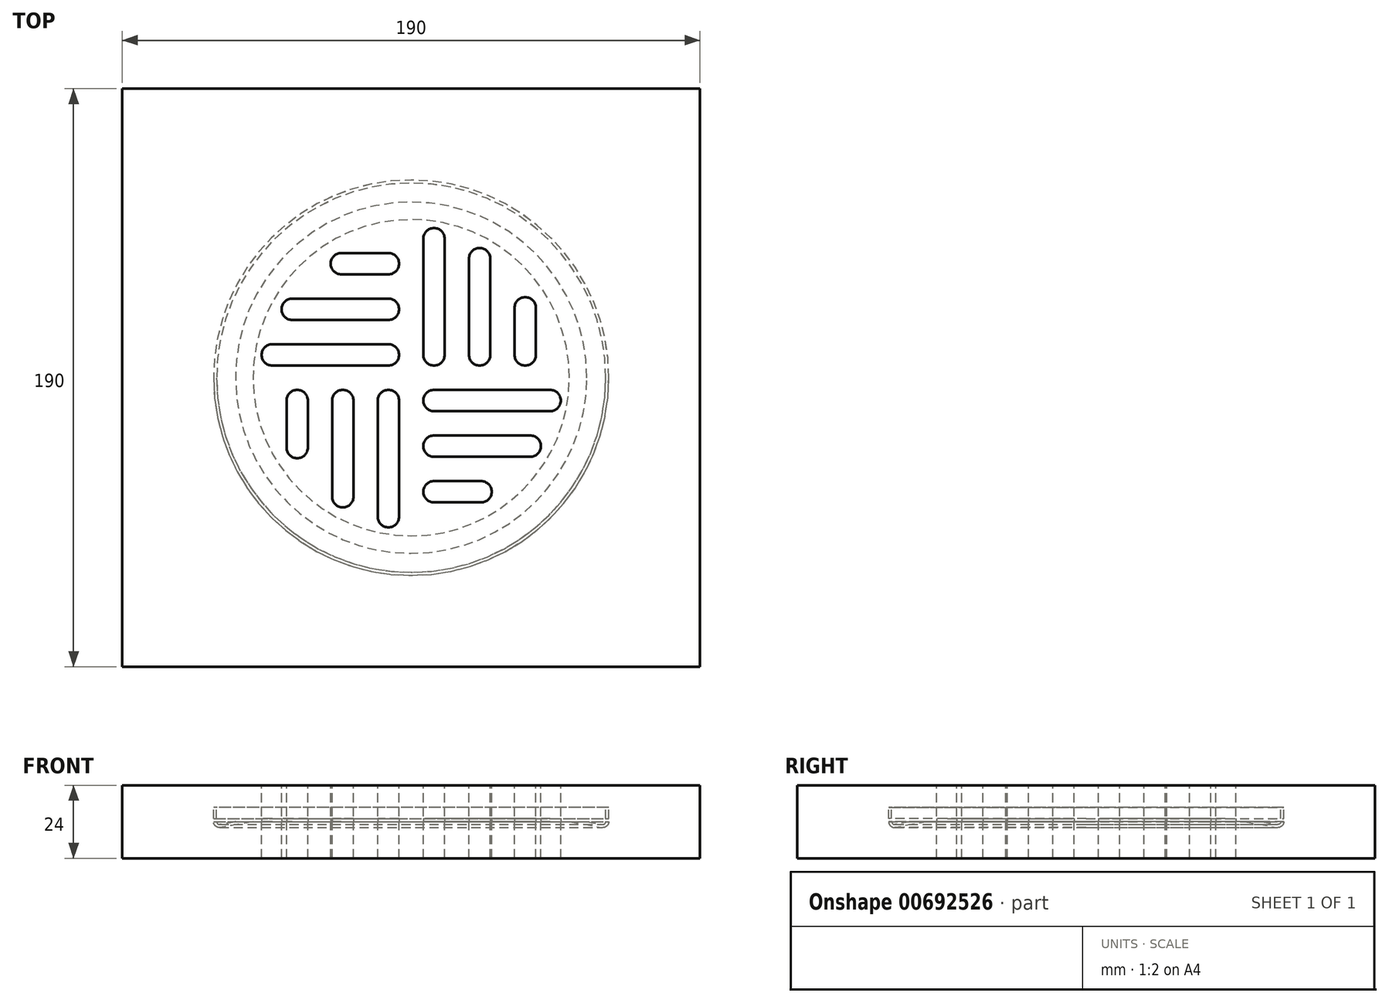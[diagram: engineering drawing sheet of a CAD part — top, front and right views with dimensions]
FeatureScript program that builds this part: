
annotation { "Feature Type Name" : "Feature", "Feature Type Description" : "" }
export const myFeature = defineFeature(function(context is Context, id is Id, definition is map)
    precondition{}
    {
        {
            var Q0;
            Q0=qCreatedBy(makeId("Top.planeOp"),FACE);
            var sketch = newSketch(context, id + "F0", { "sketchPlane" : qUnion([Q0])});
            skLineSegment(sketch, "E0", {"start": v(20.45, 0) * mm, "end": v(50.59, 0) * mm});
            skLineSegment(sketch, "E1", {"start": v(50.59, 0) * mm, "end": v(50.59, 2.78) * mm});
            skLineSegment(sketch, "E2", {"start": v(20.45, 0) * mm, "end": v(20.45, 3.6) * mm});
            skLineSegment(sketch, "E3", {"start": v(20.45, 3.6) * mm, "end": v(16.3, 3.6) * mm});
            skLineSegment(sketch, "E4", {"start": v(16.3, 3.6) * mm, "end": v(16.3, 7.46) * mm});
            skLineSegment(sketch, "E5", {"start": v(16.3, 7.46) * mm, "end": v(12.16, 7.46) * mm});
            skLineSegment(sketch, "E6.0", {"start": v(16.9, 8.06) * mm, "end": v(12.16, 8.06) * mm});
            skLineSegment(sketch, "E6.1", {"start": v(16.9, 4.2) * mm, "end": v(16.9, 8.06) * mm});
            skLineSegment(sketch, "E6.2", {"start": v(49.99, 0.6) * mm, "end": v(49.99, 2.78) * mm});
            skLineSegment(sketch, "E6.3", {"start": v(21.05, 0.6) * mm, "end": v(49.99, 0.6) * mm});
            skLineSegment(sketch, "E6.4", {"start": v(21.05, 0.6) * mm, "end": v(21.05, 4.2) * mm});
            skLineSegment(sketch, "E6.5", {"start": v(21.05, 4.2) * mm, "end": v(16.9, 4.2) * mm});
            skLineSegment(sketch, "E7", {"start": v(12.16, 8.06) * mm, "end": v(12.16, 7.46) * mm});
            skLineSegment(sketch, "E8", {"start": v(49.99, 2.78) * mm, "end": v(50.59, 2.78) * mm});
            skSolve(sketch);
        }
        {
            var Q0;
            Q0=qCreatedBy(makeId("Top.planeOp"),FACE);
            var sketch = newSketch(context, id + "F1", { "sketchPlane" : qUnion([Q0])});
            skLineSegment(sketch, "E9", {"start": v(0, 12.91) * mm, "end": v(0, -2.1) * mm, "construction": true});
            skSolve(sketch);
        }
        {
            var Q0;
            Q0=makeQuery(id+"F0.imprint","IMPRINT",FACE,{"disambiguationData":[TD([[makeQuery(id+"F0.imprint","IMPRINT",EDGE,{"derivedFrom":sQuery(id+"F0.wireOp",EDGE,"E0")}),1.0]])]});
            var Q1;
            Q1=sQuery(id+"F1.wireOp",EDGE,"E9");
            revolve(context, id + "F2", {"entities" : qUnion([Q0]), "axis" : qUnion([Q1]), "revolveType" : RevolveType.FULL});
        }
        {
            var Q0;
            Q0=makeQuery(id+"F2.opRevolve","SWEPT_BODY",BODY,{"disambiguationData":[OSD([sQuery(id+"F0.wireOp",EDGE,"E0"),sQuery(id+"F0.wireOp",EDGE,"E1"),sQuery(id+"F0.wireOp",EDGE,"E2"),sQuery(id+"F0.wireOp",EDGE,"E3"),sQuery(id+"F0.wireOp",EDGE,"E4"),sQuery(id+"F0.wireOp",EDGE,"E5"),sQuery(id+"F0.wireOp",EDGE,"E6.0"),sQuery(id+"F0.wireOp",EDGE,"E6.1"),sQuery(id+"F0.wireOp",EDGE,"E6.2"),sQuery(id+"F0.wireOp",EDGE,"E6.3"),sQuery(id+"F0.wireOp",EDGE,"E6.4"),sQuery(id+"F0.wireOp",EDGE,"E6.5"),sQuery(id+"F0.wireOp",EDGE,"E7"),sQuery(id+"F0.wireOp",EDGE,"E8")])]});
            deleteBodies(context, id + "F3", {"entities" : qUnion([Q0])});
        }
        {
            var Q0;
            Q0=qCreatedBy(makeId("Front.planeOp"),FACE);
            var sketch = newSketch(context, id + "F4", { "sketchPlane" : qUnion([Q0])});
            skLineSegment(sketch, "E10", {"start": v(0, 57.85) * mm, "end": v(0, -62.15) * mm, "construction": true});
            skLineSegment(sketch, "E11", {"start": v(-52, 0) * mm, "end": v(0, 0) * mm});
            skLineSegment(sketch, "E12", {"start": v(-52, 0) * mm, "end": v(-62.65, -1.88) * mm});
            skLineSegment(sketch, "E13", {"start": v(-65, 4.7) * mm, "end": v(-65, 0.1) * mm});
            skPoint(sketch, "E14.visualSharp", {"position": v(-65, -2.3) * mm});
            skArc(sketch, "E14.filletArc", {"start": v(-65, 0.1) * mm, "mid": v(-64.29, -1.44) * mm, "end": v(-62.65, -1.88) * mm});
            skLineSegment(sketch, "E15.0", {"start": v(-52.09, 1) * mm, "end": v(0, 1) * mm});
            skLineSegment(sketch, "E15.1", {"start": v(-52.09, 1) * mm, "end": v(-62.83, -0.9) * mm});
            skLineSegment(sketch, "E15.2", {"start": v(-64, 4.7) * mm, "end": v(-64, 0.1) * mm});
            skPoint(sketch, "E16.visualSharp", {"position": v(-64, -1.1) * mm});
            skArc(sketch, "E16.filletArc", {"start": v(-64, 0.1) * mm, "mid": v(-63.64, -0.67) * mm, "end": v(-62.83, -0.9) * mm});
            skLineSegment(sketch, "E17", {"start": v(-65, 4.7) * mm, "end": v(-64, 4.7) * mm});
            skLineSegment(sketch, "E18", {"start": v(0, 1) * mm, "end": v(0, 0) * mm});
            skSolve(sketch);
        }
        {
            var Q0;
            Q0=qSketchRegion(id+"F4",true);
            var Q1;
            Q1=sQuery(id+"F4.wireOp",EDGE,"E10");
            revolve(context, id + "F5", {"entities" : qUnion([Q0]), "axis" : qUnion([Q1]), "revolveType" : RevolveType.FULL});
        }
        {
            var Q0;
            Q0=makeQuery(id+"F5.opRevolve","SWEPT_FACE",FACE,{"disambiguationData":[OSD([sQuery(id+"F4.wireOp",EDGE,"E11")])]});
            var sketch = newSketch(context, id + "F6", { "sketchPlane" : qUnion([Q0])});
            skLineSegment(sketch, "E19.left", {"start": v(-11, 45.7) * mm, "end": v(-11, 7.5) * mm});
            skLineSegment(sketch, "E19.right", {"start": v(-4, 45.7) * mm, "end": v(-4, 7.5) * mm});
            skLineSegment(sketch, "E20", {"start": v(0, 53.56) * mm, "end": v(0, -45.34) * mm, "construction": true});
            skArc(sketch, "E21", {"start": v(-11, 45.7) * mm, "mid": v(-7.5, 49.2) * mm, "end": v(-4, 45.7) * mm});
            skArc(sketch, "E22", {"start": v(-11, 7.5) * mm, "mid": v(-7.5, 4) * mm, "end": v(-4, 7.5) * mm});
            skLineSegment(sketch, "E23", {"start": v(-6.59, 4.12) * mm, "end": v(-8.41, 4.12) * mm, "construction": true});
            skLineSegment(sketch, "E24.left", {"start": v(-26, 39.15) * mm, "end": v(-26, 7.5) * mm});
            skLineSegment(sketch, "E24.right", {"start": v(-19, 39.15) * mm, "end": v(-19, 7.5) * mm});
            skLineSegment(sketch, "E25.left", {"start": v(-41, 22.98) * mm, "end": v(-41, 7.5) * mm});
            skLineSegment(sketch, "E25.right", {"start": v(-34, 22.98) * mm, "end": v(-34, 7.5) * mm});
            skArc(sketch, "E26", {"start": v(-26, 39.15) * mm, "mid": v(-22.5, 42.65) * mm, "end": v(-19, 39.15) * mm});
            skArc(sketch, "E27", {"start": v(-26, 7.5) * mm, "mid": v(-22.5, 4) * mm, "end": v(-19, 7.5) * mm});
            skArc(sketch, "E28", {"start": v(-34, 22.98) * mm, "mid": v(-37.5, 26.48) * mm, "end": v(-41, 22.98) * mm});
            skArc(sketch, "E29", {"start": v(-34, 7.5) * mm, "mid": v(-37.5, 4) * mm, "end": v(-41, 7.5) * mm});
            skLineSegment(sketch, "E30.trimOffspring", {"start": v(-21.59, 4.12) * mm, "end": v(-23.41, 4.12) * mm, "construction": true});
            skLineSegment(sketch, "E31.trimOffspring", {"start": v(-36.59, 4.12) * mm, "end": v(-38.41, 4.12) * mm, "construction": true});
            skArc(sketch, "E32.1.0", {"start": v(-45.7, -11) * mm, "mid": v(-49.2, -7.5) * mm, "end": v(-45.7, -4) * mm});
            skLineSegment(sketch, "E32.1.1", {"start": v(-45.7, -11) * mm, "end": v(-7.5, -11) * mm});
            skLineSegment(sketch, "E32.1.2", {"start": v(-45.7, -4) * mm, "end": v(-7.5, -4) * mm});
            skArc(sketch, "E32.1.3", {"start": v(-7.5, -11) * mm, "mid": v(-4, -7.5) * mm, "end": v(-7.5, -4) * mm});
            skLineSegment(sketch, "E32.1.4", {"start": v(-39.15, -19) * mm, "end": v(-7.5, -19) * mm});
            skLineSegment(sketch, "E32.1.5", {"start": v(-39.15, -26) * mm, "end": v(-7.5, -26) * mm});
            skArc(sketch, "E32.1.6", {"start": v(-39.15, -26) * mm, "mid": v(-42.65, -22.5) * mm, "end": v(-39.15, -19) * mm});
            skArc(sketch, "E32.1.7", {"start": v(-7.5, -26) * mm, "mid": v(-4, -22.5) * mm, "end": v(-7.5, -19) * mm});
            skLineSegment(sketch, "E32.1.8", {"start": v(-4.12, -36.59) * mm, "end": v(-4.12, -38.41) * mm, "construction": true});
            skLineSegment(sketch, "E32.1.9", {"start": v(-22.98, -34) * mm, "end": v(-7.5, -34) * mm});
            skArc(sketch, "E32.1.10", {"start": v(-7.5, -34) * mm, "mid": v(-4, -37.5) * mm, "end": v(-7.5, -41) * mm});
            skLineSegment(sketch, "E32.1.11", {"start": v(-22.98, -41) * mm, "end": v(-7.5, -41) * mm});
            skArc(sketch, "E32.1.12", {"start": v(-22.98, -34) * mm, "mid": v(-26.48, -37.5) * mm, "end": v(-22.98, -41) * mm});
            skArc(sketch, "E32.2.0", {"start": v(11, -45.7) * mm, "mid": v(7.5, -49.2) * mm, "end": v(4, -45.7) * mm});
            skLineSegment(sketch, "E32.2.1", {"start": v(11, -45.7) * mm, "end": v(11, -7.5) * mm});
            skLineSegment(sketch, "E32.2.2", {"start": v(4, -45.7) * mm, "end": v(4, -7.5) * mm});
            skArc(sketch, "E32.2.3", {"start": v(11, -7.5) * mm, "mid": v(7.5, -4) * mm, "end": v(4, -7.5) * mm});
            skLineSegment(sketch, "E32.2.4", {"start": v(19, -39.15) * mm, "end": v(19, -7.5) * mm});
            skLineSegment(sketch, "E32.2.5", {"start": v(26, -39.15) * mm, "end": v(26, -7.5) * mm});
            skArc(sketch, "E32.2.6", {"start": v(26, -39.15) * mm, "mid": v(22.5, -42.65) * mm, "end": v(19, -39.15) * mm});
            skArc(sketch, "E32.2.7", {"start": v(26, -7.5) * mm, "mid": v(22.5, -4) * mm, "end": v(19, -7.5) * mm});
            skLineSegment(sketch, "E32.2.8", {"start": v(36.59, -4.12) * mm, "end": v(38.41, -4.12) * mm, "construction": true});
            skLineSegment(sketch, "E32.2.9", {"start": v(34, -22.98) * mm, "end": v(34, -7.5) * mm});
            skArc(sketch, "E32.2.10", {"start": v(34, -7.5) * mm, "mid": v(37.5, -4) * mm, "end": v(41, -7.5) * mm});
            skLineSegment(sketch, "E32.2.11", {"start": v(41, -22.98) * mm, "end": v(41, -7.5) * mm});
            skArc(sketch, "E32.2.12", {"start": v(34, -22.98) * mm, "mid": v(37.5, -26.48) * mm, "end": v(41, -22.98) * mm});
            skArc(sketch, "E32.3.0", {"start": v(45.7, 11) * mm, "mid": v(49.2, 7.5) * mm, "end": v(45.7, 4) * mm});
            skLineSegment(sketch, "E32.3.1", {"start": v(45.7, 11) * mm, "end": v(7.5, 11) * mm});
            skLineSegment(sketch, "E32.3.2", {"start": v(45.7, 4) * mm, "end": v(7.5, 4) * mm});
            skArc(sketch, "E32.3.3", {"start": v(7.5, 11) * mm, "mid": v(4, 7.5) * mm, "end": v(7.5, 4) * mm});
            skLineSegment(sketch, "E32.3.4", {"start": v(39.15, 19) * mm, "end": v(7.5, 19) * mm});
            skLineSegment(sketch, "E32.3.5", {"start": v(39.15, 26) * mm, "end": v(7.5, 26) * mm});
            skArc(sketch, "E32.3.6", {"start": v(39.15, 26) * mm, "mid": v(42.65, 22.5) * mm, "end": v(39.15, 19) * mm});
            skArc(sketch, "E32.3.7", {"start": v(7.5, 26) * mm, "mid": v(4, 22.5) * mm, "end": v(7.5, 19) * mm});
            skLineSegment(sketch, "E32.3.8", {"start": v(4.12, 36.59) * mm, "end": v(4.12, 38.41) * mm, "construction": true});
            skLineSegment(sketch, "E32.3.9", {"start": v(22.98, 34) * mm, "end": v(7.5, 34) * mm});
            skArc(sketch, "E32.3.10", {"start": v(7.5, 34) * mm, "mid": v(4, 37.5) * mm, "end": v(7.5, 41) * mm});
            skLineSegment(sketch, "E32.3.11", {"start": v(22.98, 41) * mm, "end": v(7.5, 41) * mm});
            skArc(sketch, "E32.3.12", {"start": v(22.98, 34) * mm, "mid": v(26.48, 37.5) * mm, "end": v(22.98, 41) * mm});
            skPoint(sketch, "E32.center", {"position": v(0, 0) * mm});
            skLineSegment(sketch, "E33.bottom", {"start": v(95, 95) * mm, "end": v(-95, 95) * mm});
            skLineSegment(sketch, "E33.top", {"start": v(95, -95) * mm, "end": v(-95, -95) * mm});
            skLineSegment(sketch, "E33.left", {"start": v(95, 95) * mm, "end": v(95, -95) * mm});
            skLineSegment(sketch, "E33.right", {"start": v(-95, 95) * mm, "end": v(-95, -95) * mm});
            skSolve(sketch);
        }
        {
            var Q0;
            Q0=qSketchRegion(id+"F6",true);
            extrude(context, id + "F7", {"entities" : qUnion([Q0]), "operationType" : NewBodyOperationType.REMOVE, "oppositeDirection" : true, "depth" : 1 * mm});
        }
        {
            var Q0;
            Q0 = qSketchRegion(id + "F6", true);
            extrude(context, id + "F8", {"entities" : qUnion([Q0]), "endBound" : BoundingType.SYMMETRIC, "depth" : 24 * mm, "offsetDistance" : 25 * mm});
        }
    });
